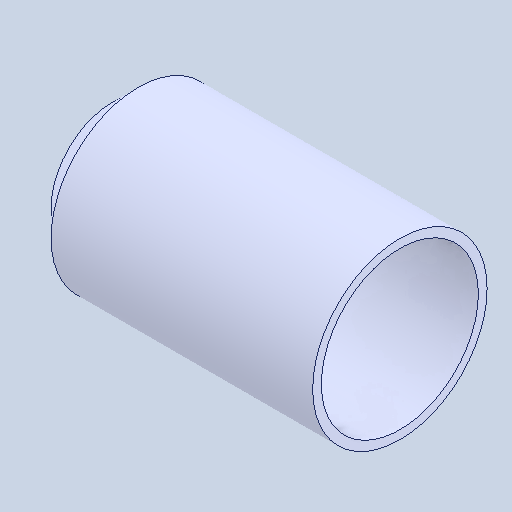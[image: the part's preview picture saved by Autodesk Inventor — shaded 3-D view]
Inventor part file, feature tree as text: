
AUTODESK INVENTOR PART (.ipt)
format: ipt  version: 2024.1 (Build 281209000, 209)  size: 114,176 bytes
history: native  units: in
note: dims shown in document units (in); Inventor stores cm internally (conversion verified against a paired STEP export)
features: revolve x1
ambient origin geometry x8: Origin, YZ Plane, XZ Plane, XY Plane, X Axis, Y Axis, Z Axis, Center Point
bodies: Solid1 (feature_tree)
feature tree (1):
  revolve  "Revolve1"  [1 undecoded]
note: 1 required parameter value undecoded (feature->parameter linkage not recoverable at this tier; creation-order binding heuristic only, values carry confidence <= 0.55)
